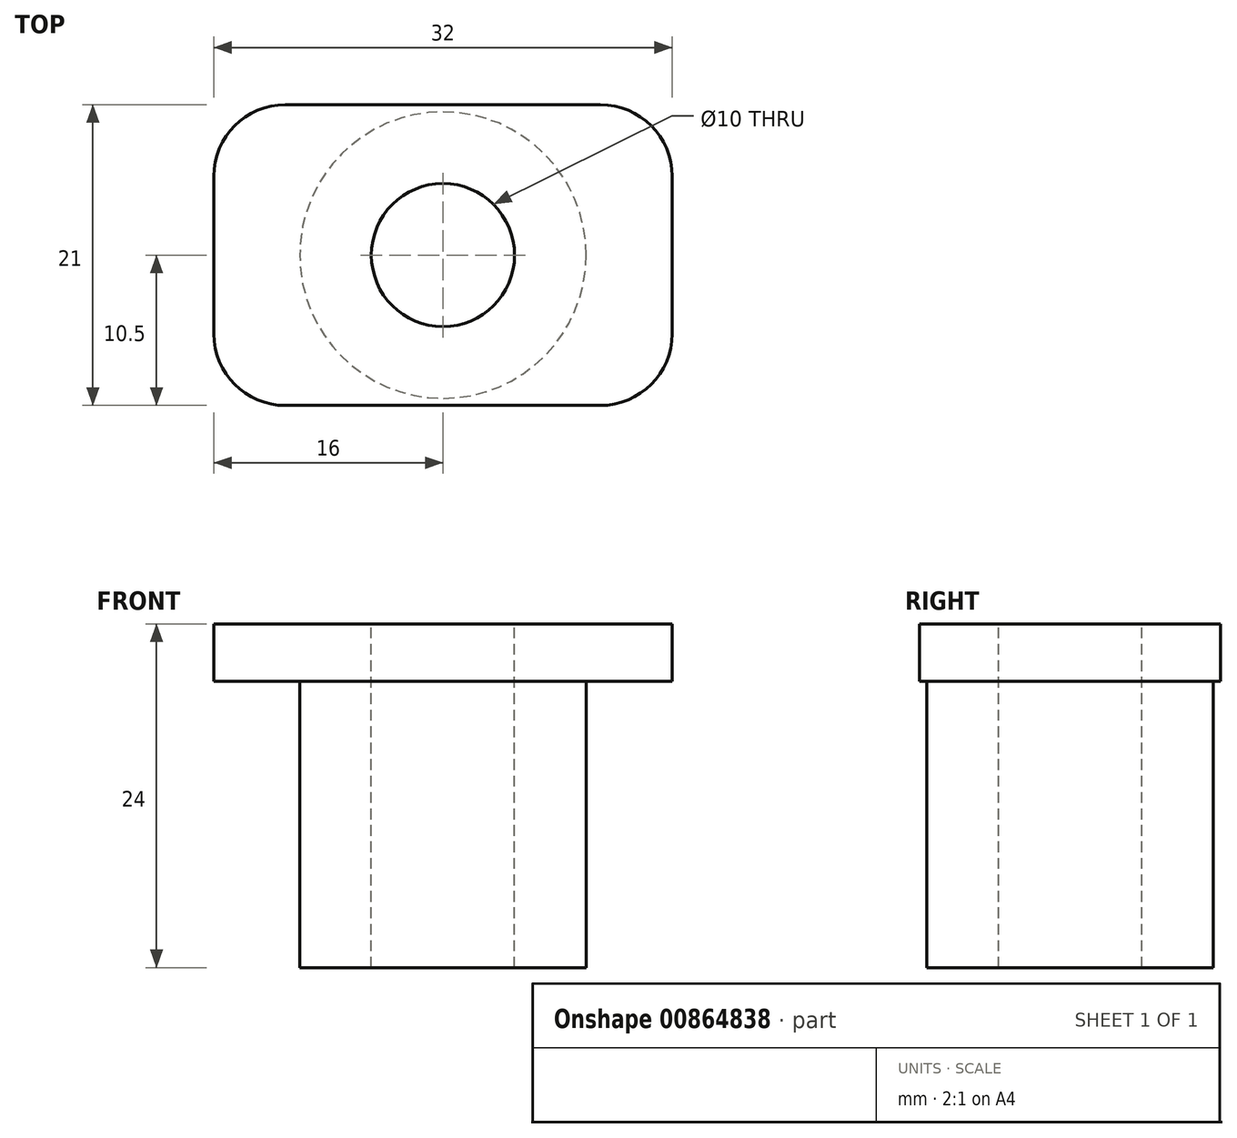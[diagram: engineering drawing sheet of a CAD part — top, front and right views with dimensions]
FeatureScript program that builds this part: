
annotation { "Feature Type Name" : "Feature", "Feature Type Description" : "" }
export const myFeature = defineFeature(function(context is Context, id is Id, definition is map)
    precondition{}
    {
        {
            var Q0;
            Q0=qCreatedBy(makeId("Top.planeOp"),FACE);
            var sketch = newSketch(context, id + "F0", { "sketchPlane" : qUnion([Q0])});
            skCircle(sketch, "E0", {"center": v(0, 0) * mm, "radius": 10 * mm});
            skSolve(sketch);
        }
        {
            var Q0;
            Q0=makeQuery(id+"F0.imprint","IMPRINT",FACE,{"disambiguationData":[TD([[makeQuery(id+"F0.imprint","IMPRINT",EDGE,{"derivedFrom":sQuery(id+"F0.wireOp",EDGE,"E0")}),1.0]])]});
            extrude(context, id + "F1", {"entities" : qUnion([Q0]), "depth" : 20 * mm, "offsetDistance" : 25 * mm});
        }
        {
            var Q0;
            Q0=makeQuery(id+"F1.opExtrude","CAP_FACE",FACE,{"disambiguationData":[OSD([sQuery(id+"F0.wireOp",EDGE,"E0")])],"isStart":false});
            var sketch = newSketch(context, id + "F2", { "sketchPlane" : qUnion([Q0])});
            skLineSegment(sketch, "E1.bottom", {"start": v(16, -10.5) * mm, "end": v(-16, -10.5) * mm});
            skLineSegment(sketch, "E1.top", {"start": v(16, 10.5) * mm, "end": v(-16, 10.5) * mm});
            skLineSegment(sketch, "E1.left", {"start": v(16, -10.5) * mm, "end": v(16, 10.5) * mm});
            skLineSegment(sketch, "E1.right", {"start": v(-16, -10.5) * mm, "end": v(-16, 10.5) * mm});
            skPoint(sketch, "E1.middle", {"position": v(0, 0) * mm});
            skSolve(sketch);
        }
        {
            var Q0;
            Q0 = qSketchRegion(id + "F2", true);
            extrude(context, id + "F3", {"entities" : qUnion([Q0]), "operationType" : NewBodyOperationType.ADD, "depth" : 4 * mm, "offsetDistance" : 25 * mm});
        }
        {
            var Q0;
            Q0=makeQuery(id+"F3.opExtrude","CAP_FACE",FACE,{"disambiguationData":[OSD([sQuery(id+"F2.wireOp",EDGE,"E1.bottom"),sQuery(id+"F2.wireOp",EDGE,"E1.top"),sQuery(id+"F2.wireOp",EDGE,"E1.left"),sQuery(id+"F2.wireOp",EDGE,"E1.right")])],"isStart":false});
            var sketch = newSketch(context, id + "F4", { "sketchPlane" : qUnion([Q0])});
            skCircle(sketch, "E2", {"center": v(0, 0) * mm, "radius": 5 * mm});
            skSolve(sketch);
        }
        {
            var Q0;
            Q0=makeQuery(id+"F4.imprint","IMPRINT",FACE,{"disambiguationData":[TD([[makeQuery(id+"F4.imprint","IMPRINT",EDGE,{"derivedFrom":sQuery(id+"F4.wireOp",EDGE,"E2")}),1.0]])]});
            extrude(context, id + "F5", {"entities" : qUnion([Q0]), "operationType" : NewBodyOperationType.REMOVE, "oppositeDirection" : true, "depth" : 25 * mm, "offsetDistance" : 25 * mm});
        }
        {
            var Q0;
            Q0=makeQuery(id+"F3.opExtrude","SWEPT_EDGE",EDGE,{"disambiguationData":[OSD([sQuery(id+"F2.wireOp",EDGE,"E1.top"),sQuery(id+"F2.wireOp",EDGE,"E1.left")])]});
            var Q1;
            Q1=makeQuery(id+"F3.opExtrude","SWEPT_EDGE",EDGE,{"disambiguationData":[OSD([sQuery(id+"F2.wireOp",EDGE,"E1.top"),sQuery(id+"F2.wireOp",EDGE,"E1.right")])]});
            var Q2;
            Q2=makeQuery(id+"F3.opExtrude","SWEPT_EDGE",EDGE,{"disambiguationData":[OSD([sQuery(id+"F2.wireOp",EDGE,"E1.bottom"),sQuery(id+"F2.wireOp",EDGE,"E1.right")])]});
            var Q3;
            Q3=makeQuery(id+"F3.opExtrude","SWEPT_EDGE",EDGE,{"disambiguationData":[OSD([sQuery(id+"F2.wireOp",EDGE,"E1.bottom"),sQuery(id+"F2.wireOp",EDGE,"E1.left")])]});
            fillet(context, id + "F6", {"entities" : qUnion([Q0, Q1, Q2, Q3]), "radius" : 5 * mm, "tangentPropagation" : true, "allowEdgeOverflow" : false});
        }
    });
